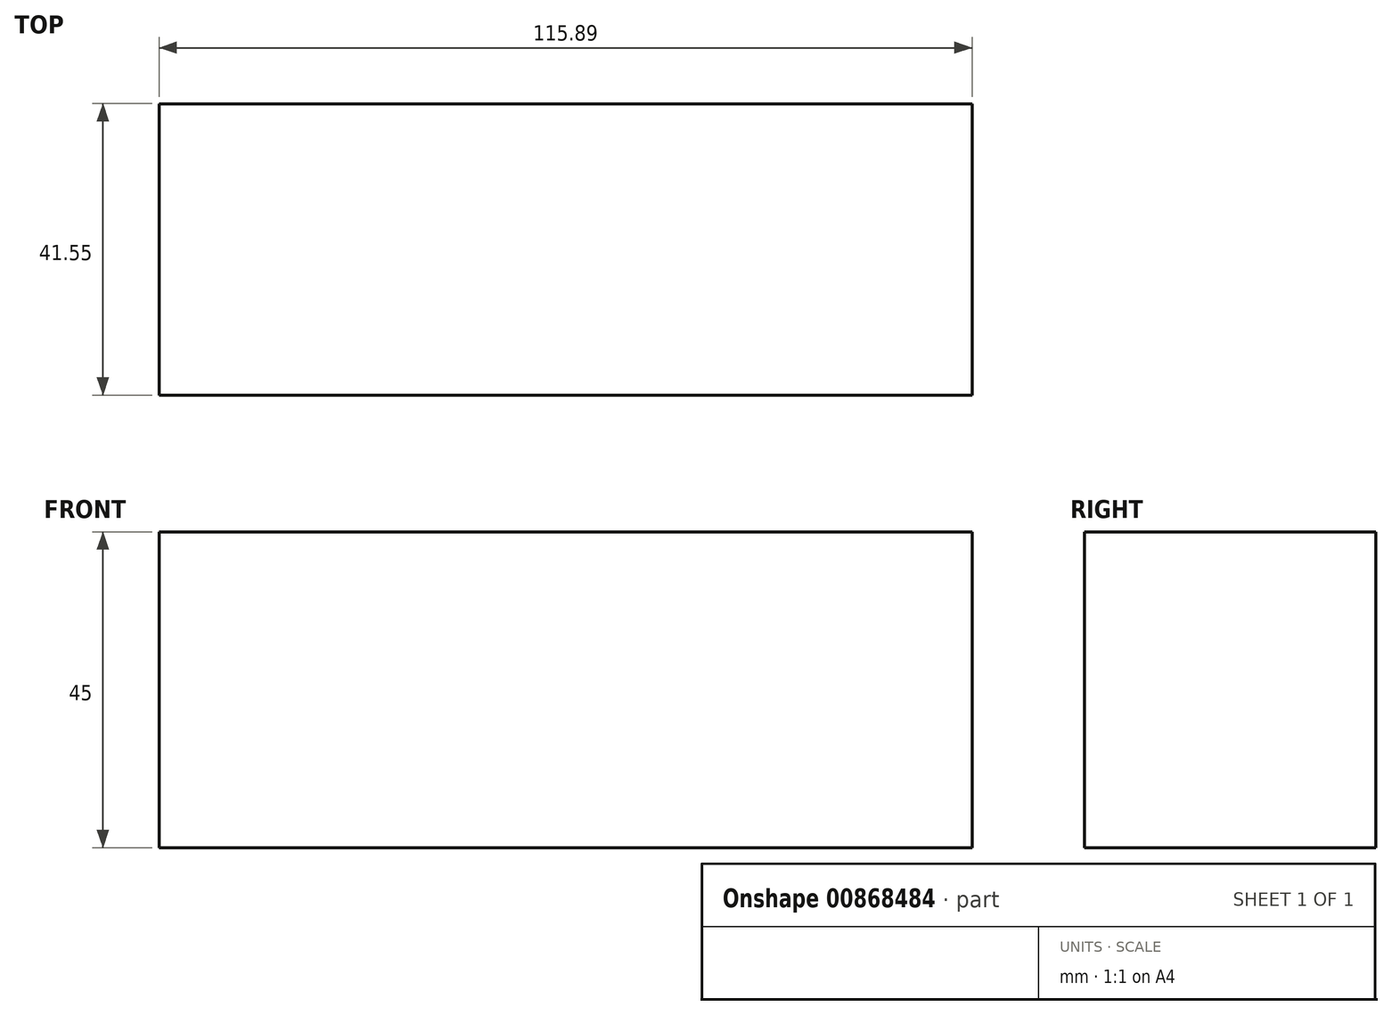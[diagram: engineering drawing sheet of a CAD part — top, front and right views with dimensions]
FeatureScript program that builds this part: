
annotation { "Feature Type Name" : "Feature", "Feature Type Description" : "" }
export const myFeature = defineFeature(function(context is Context, id is Id, definition is map)
    precondition{}
    {
        {
            var Q0;
            Q0=qCreatedBy(makeId("Top.planeOp"),FACE);
            var sketch = newSketch(context, id + "F0", { "sketchPlane" : qUnion([Q0])});
            skLineSegment(sketch, "E0.bottom", {"start": v(-59.23, 41.55) * mm, "end": v(56.66, 41.55) * mm});
            skLineSegment(sketch, "E0.top", {"start": v(-59.23, 0) * mm, "end": v(56.66, 0) * mm});
            skLineSegment(sketch, "E0.left", {"start": v(-59.23, 41.55) * mm, "end": v(-59.23, 0) * mm});
            skLineSegment(sketch, "E0.right", {"start": v(56.66, 41.55) * mm, "end": v(56.66, 0) * mm});
            skSolve(sketch);
        }
        {
            var Q0;
            Q0 = qSketchRegion(id + "F0", true);
            extrude(context, id + "F1", {"entities" : qUnion([Q0]), "depth" : 45 * mm, "offsetDistance" : 25.4 * mm});
        }
    });
